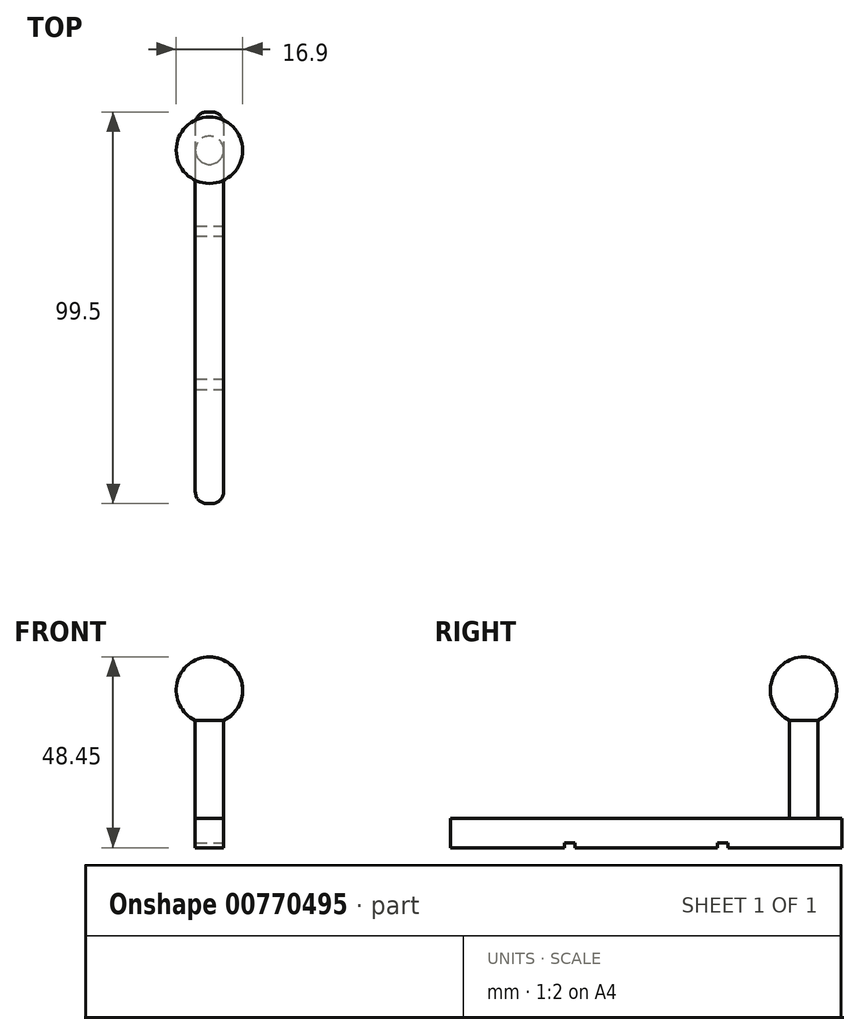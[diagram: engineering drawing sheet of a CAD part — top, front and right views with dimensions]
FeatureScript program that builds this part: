
annotation { "Feature Type Name" : "Feature", "Feature Type Description" : "" }
export const myFeature = defineFeature(function(context is Context, id is Id, definition is map)
    precondition{}
    {
        {
            var Q0;
            Q0=qCreatedBy(makeId("Top.planeOp"),FACE);
            var sketch = newSketch(context, id + "F0", { "sketchPlane" : qUnion([Q0])});
            skLineSegment(sketch, "E0.bottom", {"start": v(0.6, 49.75) * mm, "end": v(-0.6, 49.75) * mm});
            skLineSegment(sketch, "E0.top", {"start": v(0.6, -49.75) * mm, "end": v(-0.6, -49.75) * mm});
            skLineSegment(sketch, "E0.left", {"start": v(3.6, 46.75) * mm, "end": v(3.6, -46.75) * mm});
            skLineSegment(sketch, "E0.right", {"start": v(-3.6, 46.75) * mm, "end": v(-3.6, -46.75) * mm});
            skPoint(sketch, "E0.middle", {"position": v(0, 0) * mm});
            skPoint(sketch, "E1.visualSharp", {"position": v(3.6, 49.75) * mm});
            skArc(sketch, "E1.filletArc", {"start": v(3.6, 46.75) * mm, "mid": v(2.72, 48.87) * mm, "end": v(0.6, 49.75) * mm});
            skPoint(sketch, "E2.visualSharp", {"position": v(-3.6, 49.75) * mm});
            skArc(sketch, "E2.filletArc", {"start": v(-0.6, 49.75) * mm, "mid": v(-2.72, 48.87) * mm, "end": v(-3.6, 46.75) * mm});
            skPoint(sketch, "E3.visualSharp", {"position": v(3.6, -49.75) * mm});
            skArc(sketch, "E3.filletArc", {"start": v(0.6, -49.75) * mm, "mid": v(2.72, -48.87) * mm, "end": v(3.6, -46.75) * mm});
            skPoint(sketch, "E4.visualSharp", {"position": v(-3.6, -49.75) * mm});
            skArc(sketch, "E4.filletArc", {"start": v(-3.6, -46.75) * mm, "mid": v(-2.72, -48.87) * mm, "end": v(-0.6, -49.75) * mm});
            skSolve(sketch);
        }
        {
            var Q0;
            Q0=makeQuery(id+"F0.imprint","IMPRINT",FACE,{"disambiguationData":[TD([[makeQuery(id+"F0.imprint","IMPRINT",EDGE,{"derivedFrom":sQuery(id+"F0.wireOp",EDGE,"E0.bottom")}),1.0]])]});
            extrude(context, id + "F1", {"entities" : qUnion([Q0]), "depth" : 7.5 * mm, "offsetDistance" : 25 * mm});
        }
        {
            var Q0;
            Q0=makeQuery(id+"F1.opExtrude","CAP_FACE",FACE,{"disambiguationData":[OSD([sQuery(id+"F0.wireOp",EDGE,"E0.bottom"),sQuery(id+"F0.wireOp",EDGE,"E0.top"),sQuery(id+"F0.wireOp",EDGE,"E0.left"),sQuery(id+"F0.wireOp",EDGE,"E0.right"),sQuery(id+"F0.wireOp",EDGE,"E1.filletArc"),sQuery(id+"F0.wireOp",EDGE,"E2.filletArc"),sQuery(id+"F0.wireOp",EDGE,"E3.filletArc"),sQuery(id+"F0.wireOp",EDGE,"E4.filletArc")])],"isStart":true});
            var sketch = newSketch(context, id + "F2", { "sketchPlane" : qUnion([Q0])});
            skLineSegment(sketch, "E5.bottom", {"start": v(-3.6, 20.75) * mm, "end": v(3.6, 20.75) * mm});
            skLineSegment(sketch, "E5.top", {"start": v(-3.6, 18.15) * mm, "end": v(3.6, 18.15) * mm});
            skLineSegment(sketch, "E5.left", {"start": v(-3.6, 20.75) * mm, "end": v(-3.6, 18.15) * mm});
            skLineSegment(sketch, "E5.right", {"start": v(3.6, 20.75) * mm, "end": v(3.6, 18.15) * mm});
            skLineSegment(sketch, "E6.bottom", {"start": v(-3.6, -18.15) * mm, "end": v(3.6, -18.15) * mm});
            skLineSegment(sketch, "E6.top", {"start": v(-3.6, -20.75) * mm, "end": v(3.6, -20.75) * mm});
            skLineSegment(sketch, "E6.left", {"start": v(-3.6, -18.15) * mm, "end": v(-3.6, -20.75) * mm});
            skLineSegment(sketch, "E6.right", {"start": v(3.6, -18.15) * mm, "end": v(3.6, -20.75) * mm});
            skSolve(sketch);
        }
        {
            var Q0;
            Q0 = qSketchRegion(id + "F2", true);
            extrude(context, id + "F3", {"entities" : qUnion([Q0]), "operationType" : NewBodyOperationType.REMOVE, "oppositeDirection" : true, "depth" : 1.2 * mm, "offsetDistance" : 25 * mm});
        }
        {
            var Q0;
            Q0=makeQuery(id+"F1.opExtrude","CAP_FACE",FACE,{"disambiguationData":[OSD([sQuery(id+"F0.wireOp",EDGE,"E0.bottom"),sQuery(id+"F0.wireOp",EDGE,"E0.top"),sQuery(id+"F0.wireOp",EDGE,"E0.left"),sQuery(id+"F0.wireOp",EDGE,"E0.right"),sQuery(id+"F0.wireOp",EDGE,"E1.filletArc"),sQuery(id+"F0.wireOp",EDGE,"E2.filletArc"),sQuery(id+"F0.wireOp",EDGE,"E3.filletArc"),sQuery(id+"F0.wireOp",EDGE,"E4.filletArc")])],"isStart":false});
            var sketch = newSketch(context, id + "F4", { "sketchPlane" : qUnion([Q0])});
            skCircle(sketch, "E7", {"center": v(0, 40) * mm, "radius": 3.6 * mm});
            skSolve(sketch);
        }
        {
            var Q0;
            Q0 = qSketchRegion(id + "F4", true);
            extrude(context, id + "F5", {"entities" : qUnion([Q0]), "operationType" : NewBodyOperationType.ADD, "depth" : 25 * mm, "offsetDistance" : 25 * mm});
        }
        {
            var Q0;
            Q0=qCreatedBy(makeId("Front.planeOp"),FACE);
            cPlane(context, id + "F6", {"entities" : qUnion([Q0]), "cplaneType" : CPlaneType.OFFSET, "offset" : 40 * mm, "oppositeDirection" : true, "width" : 150 * mm, "height" : 150 * mm});
        }
        {
            var Q0;
            Q0=qCreatedBy(id+"F6.planeOp",FACE);
            var sketch = newSketch(context, id + "F7", { "sketchPlane" : qUnion([Q0])});
            skArc(sketch, "E8", {"start": v(0, 48.45) * mm, "mid": v(-8.45, 40) * mm, "end": v(0, 31.55) * mm});
            skLineSegment(sketch, "E9", {"start": v(0, 31.55) * mm, "end": v(0, 48.45) * mm});
            skPoint(sketch, "E10.orphan", {"position": v(0, 27.71) * mm});
            skSolve(sketch);
        }
        {
            var Q0;
            Q0 = qSketchRegion(id + "F7", true);
            var Q1;
            Q1=sQuery(id+"F7.wireOp",EDGE,"E9");
            revolve(context, id + "F8", {"operationType" : NewBodyOperationType.ADD, "surfaceOperationType" : NewSurfaceOperationType.NEW, "entities" : qUnion([Q0]), "axis" : qUnion([Q1]), "revolveType" : RevolveType.FULL});
        }
    });
